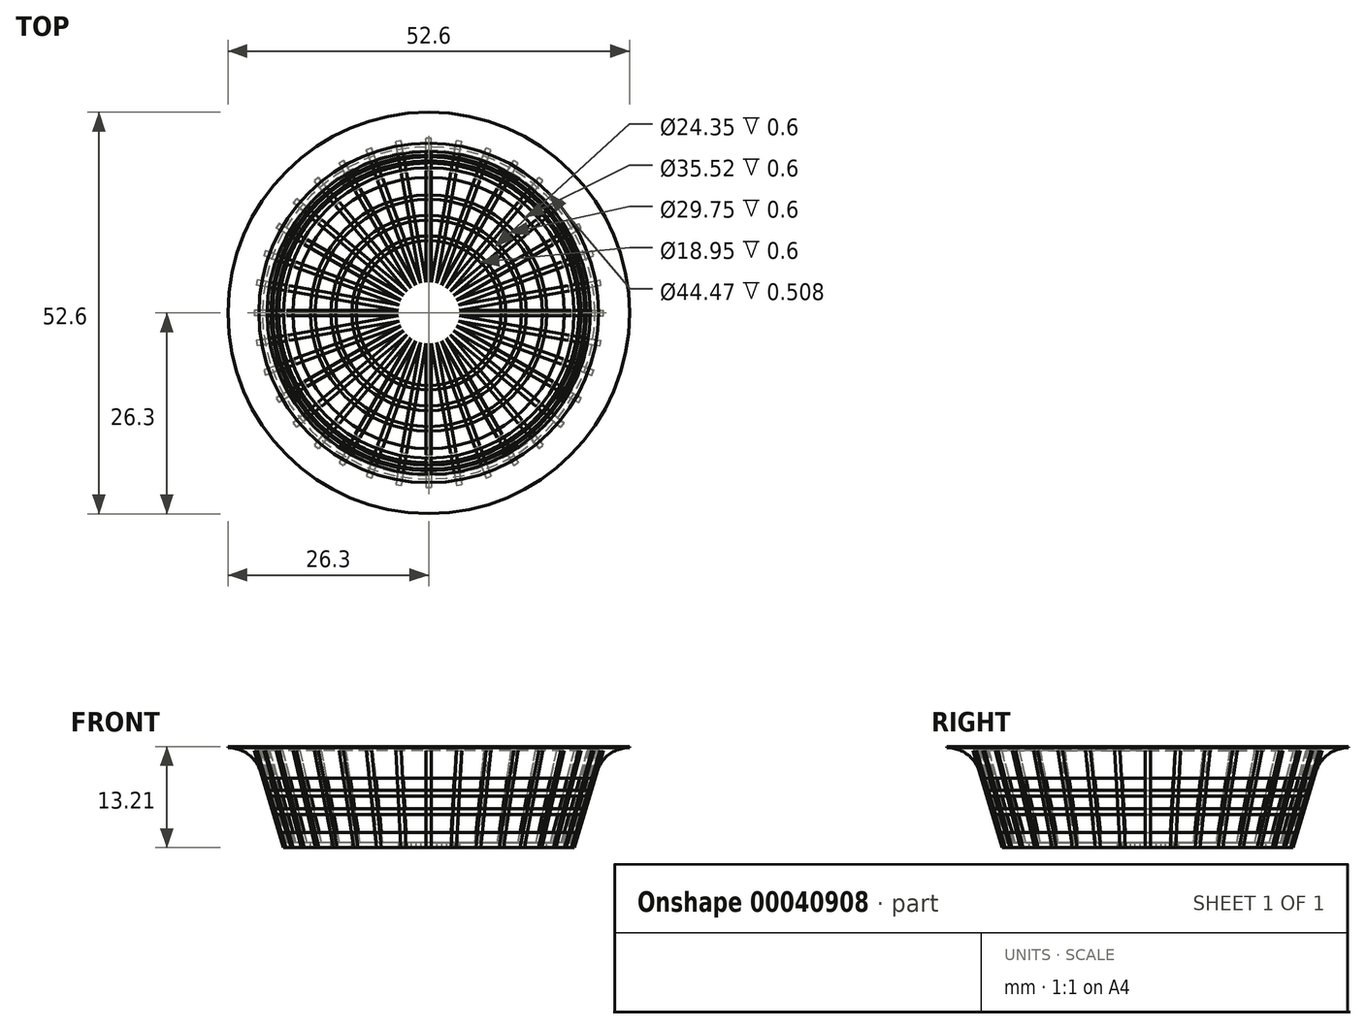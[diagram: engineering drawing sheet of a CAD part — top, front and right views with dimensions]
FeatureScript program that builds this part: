
annotation { "Feature Type Name" : "Feature", "Feature Type Description" : "" }
export const myFeature = defineFeature(function(context is Context, id is Id, definition is map)
    precondition{}
    {
        {
            var Q0;
            Q0=qCreatedBy(makeId("Top.planeOp"),FACE);
            var sketch = newSketch(context, id + "F0", { "sketchPlane" : qUnion([Q0])});
            skCircle(sketch, "E0", {"center": v(0, 0) * mm, "radius": 19.05 * mm});
            skArc(sketch, "E1", {"start": v(3.5, 18.73) * mm, "mid": v(0, 15.54) * mm, "end": v(-3.5, 18.73) * mm, "construction": true});
            skLineSegment(sketch, "E2", {"start": v(-54.09, 0) * mm, "end": v(59.61, 0) * mm, "construction": true});
            skArc(sketch, "E3.MirrorCS", {"start": v(3.5, -18.73) * mm, "mid": v(0, -15.54) * mm, "end": v(-3.5, -18.73) * mm, "construction": true});
            skSolve(sketch);
        }
        {
            var Q0;
            Q0=qCreatedBy(makeId("Top.planeOp"),FACE);
            cPlane(context, id + "F1", {"entities" : qUnion([Q0]), "cplaneType" : CPlaneType.OFFSET, "offset" : 12.7 * mm, "width" : 152.4 * mm, "height" : 152.4 * mm});
        }
        {
            var Q0;
            Q0=qCreatedBy(id+"F1.planeOp",FACE);
            var sketch = newSketch(context, id + "F2", { "sketchPlane" : qUnion([Q0])});
            skCircle(sketch, "E4", {"center": v(0, 0) * mm, "radius": 22.86 * mm});
            skSolve(sketch);
        }
        {
            var Q0;
            Q0=qCreatedBy(makeId("Front.planeOp"),FACE);
            var sketch = newSketch(context, id + "F3", { "sketchPlane" : qUnion([Q0])});
            skLineSegment(sketch, "E5", {"start": v(0, 0) * mm, "end": v(19.05, 0) * mm});
            skLineSegment(sketch, "E6", {"start": v(19.05, 0) * mm, "end": v(22.86, 12.7) * mm});
            skLineSegment(sketch, "E7.0", {"start": v(18.6, 0.6) * mm, "end": v(22.23, 12.7) * mm});
            skLineSegment(sketch, "E7.1", {"start": v(0, 0.6) * mm, "end": v(18.6, 0.6) * mm});
            skLineSegment(sketch, "E8", {"start": v(22.23, 12.7) * mm, "end": v(22.86, 12.7) * mm});
            skLineSegment(sketch, "E9", {"start": v(0, 0.6) * mm, "end": v(0, 0) * mm});
            skLineSegment(sketch, "E10", {"start": v(0, 42.06) * mm, "end": v(0, -16.67) * mm, "construction": true});
            skSolve(sketch);
        }
        {
            var Q0;
            Q0=qSketchRegion(id+"F3",true);
            extrude(context, id + "F4", {"entities" : qUnion([Q0]), "depth" : .7 * mm, "symmetric" : true});
        }
        {
            var Q0;
            Q0=makeQuery(id+"F4.opExtrude","SWEPT_BODY",BODY,{"disambiguationData":[OSD([sQuery(id+"F3.wireOp",EDGE,"E5"),sQuery(id+"F3.wireOp",EDGE,"E6"),sQuery(id+"F3.wireOp",EDGE,"E7.0"),sQuery(id+"F3.wireOp",EDGE,"E7.1"),sQuery(id+"F3.wireOp",EDGE,"E8"),sQuery(id+"F3.wireOp",EDGE,"E9")])]});
            var Q1;
            Q1=sQuery(id+"F3.wireOp",EDGE,"E10");
            circularPattern(context, id + "F5", {"operationType" : NewBodyOperationType.ADD, "entities" : qUnion([Q0]), "axis" : qUnion([Q1]), "angle" : 10 * degree, "instanceCount" : 36, "computeTransformsWithoutBuiltin" : true});
        }
        {
            var Q0;
            Q0=qCreatedBy(makeId("Front.planeOp"),FACE);
            var sketch = newSketch(context, id + "F6", { "sketchPlane" : qUnion([Q0])});
            skLineSegment(sketch, "E11.bottom", {"start": v(9.48, 0.6) * mm, "end": v(10.08, 0.6) * mm});
            skLineSegment(sketch, "E11.top", {"start": v(9.48, 0) * mm, "end": v(10.08, 0) * mm});
            skLineSegment(sketch, "E11.left", {"start": v(9.48, 0.6) * mm, "end": v(9.48, 0) * mm});
            skLineSegment(sketch, "E11.right", {"start": v(10.08, 0.6) * mm, "end": v(10.08, 0) * mm});
            skLineSegment(sketch, "E12.1.0.0", {"start": v(12.18, 0.6) * mm, "end": v(12.18, 0) * mm});
            skLineSegment(sketch, "E12.1.0.1", {"start": v(12.18, 0.6) * mm, "end": v(12.78, 0.6) * mm});
            skLineSegment(sketch, "E12.1.0.2", {"start": v(12.78, 0.6) * mm, "end": v(12.78, 0) * mm});
            skLineSegment(sketch, "E12.1.0.3", {"start": v(12.18, 0) * mm, "end": v(12.78, 0) * mm});
            skLineSegment(sketch, "E12.2.0.0", {"start": v(14.88, 0.6) * mm, "end": v(14.88, 0) * mm});
            skLineSegment(sketch, "E12.2.0.1", {"start": v(14.88, 0.6) * mm, "end": v(15.48, 0.6) * mm});
            skLineSegment(sketch, "E12.2.0.2", {"start": v(15.48, 0.6) * mm, "end": v(15.48, 0) * mm});
            skLineSegment(sketch, "E12.2.0.3", {"start": v(14.88, 0) * mm, "end": v(15.48, 0) * mm});
            skLineSegment(sketch, "E12.direction1", {"start": v(9.48, 0) * mm, "end": v(12.18, 0) * mm, "construction": true});
            skLineSegment(sketch, "E13.bottom", {"start": v(19.71, 4.3) * mm, "end": v(20.34, 4.3) * mm});
            skLineSegment(sketch, "E13.top", {"start": v(19.94, 5.06) * mm, "end": v(20.57, 5.06) * mm});
            skLineSegment(sketch, "E13.left", {"start": v(19.71, 4.3) * mm, "end": v(19.94, 5.06) * mm});
            skLineSegment(sketch, "E13.right", {"start": v(20.34, 4.3) * mm, "end": v(20.57, 5.06) * mm});
            skLineSegment(sketch, "E14.direction1", {"start": v(19.94, 5.06) * mm, "end": v(40.73, 5.06) * mm, "construction": true});
            skLineSegment(sketch, "E14.direction2", {"start": v(19.94, 5.06) * mm, "end": v(20.67, 7.5) * mm, "construction": true});
            skLineSegment(sketch, "E15.top", {"start": v(21.15, 9.08) * mm, "end": v(21.77, 9.08) * mm});
            skLineSegment(sketch, "E15.left", {"start": v(22.23, 12.7) * mm, "end": v(21.15, 9.08) * mm});
            skLineSegment(sketch, "E15.right", {"start": v(22.02, 9.9) * mm, "end": v(21.77, 9.08) * mm});
            skLineSegment(sketch, "E16.top", {"start": v(22.23, 13.2) * mm, "end": v(26.3, 13.2) * mm});
            skLineSegment(sketch, "E16.left", {"start": v(22.23, 12.7) * mm, "end": v(22.23, 13.2) * mm});
            skLineSegment(sketch, "E16.right", {"start": v(26.3, 13.2) * mm, "end": v(26.3, 13.2) * mm});
            skPoint(sketch, "E17.visualSharp", {"position": v(22.86, 12.7) * mm});
            skArc(sketch, "E17.filletArc", {"start": v(26.3, 13.08) * mm, "mid": v(23.63, 12.2) * mm, "end": v(22.02, 9.9) * mm});
            skLineSegment(sketch, "E18", {"start": v(17.76, 0.6) * mm, "end": v(17.76, 0) * mm});
            skLineSegment(sketch, "E19", {"start": v(17.76, 0) * mm, "end": v(19.05, 0) * mm});
            skLineSegment(sketch, "E20", {"start": v(19.05, 0) * mm, "end": v(19.64, 1.96) * mm});
            skLineSegment(sketch, "E21", {"start": v(19.64, 1.96) * mm, "end": v(19.01, 1.96) * mm});
            skLineSegment(sketch, "E22", {"start": v(19.01, 1.96) * mm, "end": v(18.7, 0.93) * mm});
            skLineSegment(sketch, "E23", {"start": v(18.26, 0.6) * mm, "end": v(17.76, 0.6) * mm});
            skPoint(sketch, "E24.visualSharp", {"position": v(18.6, 0.6) * mm});
            skArc(sketch, "E24.filletArc", {"start": v(18.26, 0.6) * mm, "mid": v(18.54, 0.7) * mm, "end": v(18.7, 0.93) * mm});
            skLineSegment(sketch, "E25", {"start": v(26.3, 13.2) * mm, "end": v(26.3, 13.08) * mm});
            skLineSegment(sketch, "E26", {"start": v(26.3, 13.08) * mm, "end": v(26.3, 13.08) * mm, "construction": true});
            skLineSegment(sketch, "E27.0.0.1", {"start": v(20.67, 7.5) * mm, "end": v(21.3, 7.5) * mm});
            skLineSegment(sketch, "E27.3.0.1", {"start": v(20.44, 6.73) * mm, "end": v(20.67, 7.5) * mm});
            skLineSegment(sketch, "E27.6.0.1", {"start": v(20.44, 6.73) * mm, "end": v(21.07, 6.73) * mm});
            skLineSegment(sketch, "E27.9.0.1", {"start": v(21.07, 6.73) * mm, "end": v(21.3, 7.5) * mm});
            skSolve(sketch);
        }
        {
            var Q0;
            Q0 = qSketchRegion(id + "F6", true);
            var Q1;
            Q1=sQuery(id+"F3.wireOp",EDGE,"E10");
            revolve(context, id + "F7", {"entities" : qUnion([Q0]), "axis" : qUnion([Q1]), "revolveType" : RevolveType.FULL});
        }
    });
